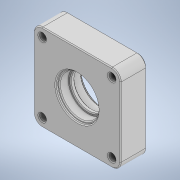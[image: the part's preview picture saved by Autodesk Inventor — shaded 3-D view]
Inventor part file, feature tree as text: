
AUTODESK INVENTOR PART (.ipt)
format: ipt  version: 2020 (Build 240168000, 168)  size: 215,040 bytes
history: native  units: in
note: dims shown in document units (in); Inventor stores cm internally (conversion verified against a paired STEP export)
features: extrude x3, chamfer x3, sketch x3, fillet x1, plane x1, mirror x1
ambient origin geometry x8: Origin, YZ Plane, XZ Plane, XY Plane, X Axis, Y Axis, Z Axis, Center Point
bodies: Solid1 (feature_tree)
feature tree (12):
  extrude  "Extrusion1"  Depth=2.5in
  fillet  "Fillet1"  Radius=0.25in
  extrude  "Extrusion2"  Depth=0.201in
  extrude  "Extrusion3"  Depth=0.75in TaperAngle=0.0deg
  plane  "Work Plane1"
  mirror  "Mirror1"
  chamfer  "Chamfer1"  Distance=0.25in
  chamfer  "Chamfer2"  Distance=1.126in
  chamfer  "Chamfer3"  Distance=0.314in
  sketch  "Sketch1"  dims[d0=2.5in d1=2.5in d2=0.25in]
  sketch  "Sketch2"  dims[d3=0.7874in d5=2.0in d6=0.7874in d8=2.0in d11=0.201in]
  sketch  "Sketch3"  dims[d12=0.998in d13=0.75in d14=0.0in d15=0.25in d16=1.126in d17=0.314in d18=0.0in d19=1.226in d20=0.064in d21=0.0in d22=0.025in d23=0.125in d24=45.0deg d25=0.025in d26=0.125in d27=45.0deg d28=0.025in d29=0.125in d30=45.0deg]
